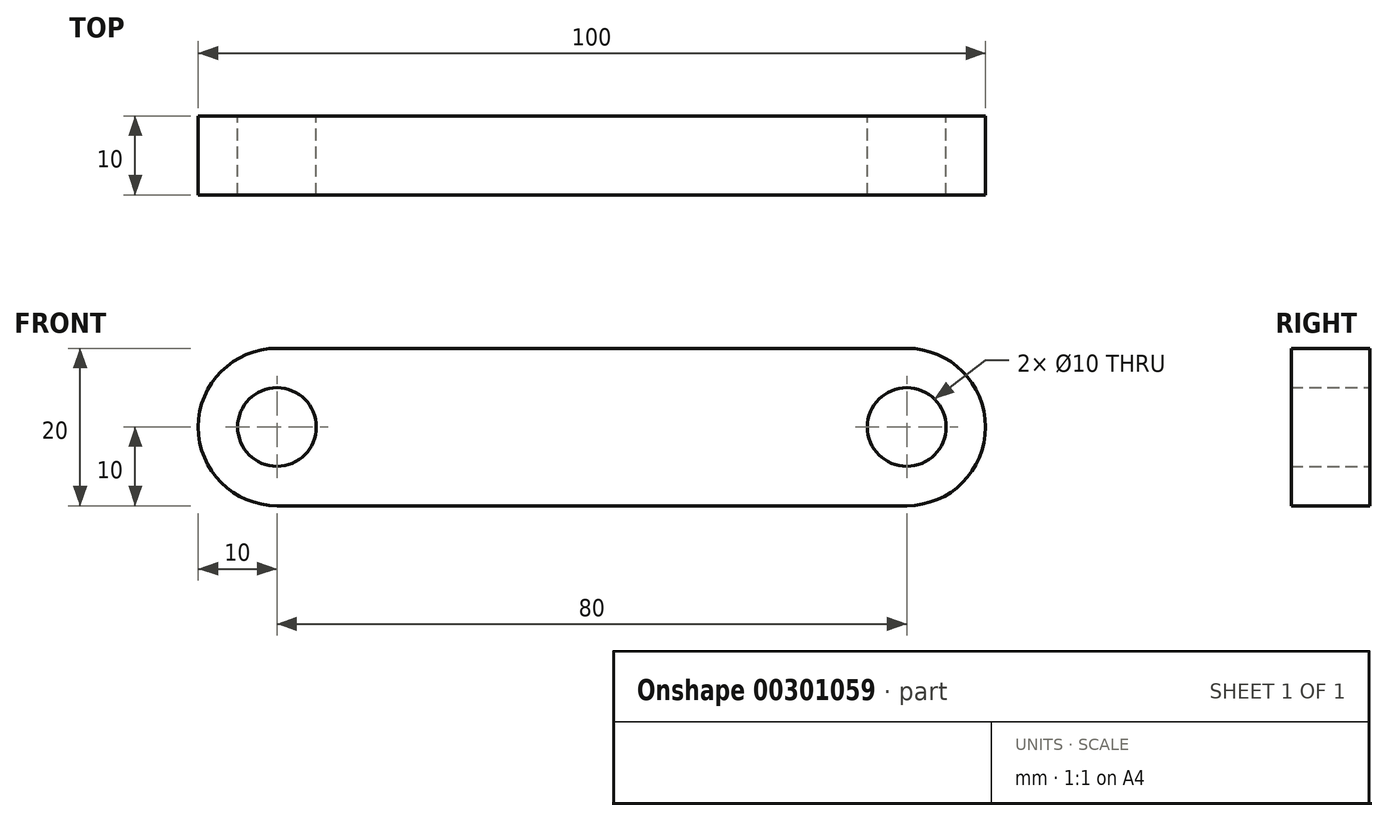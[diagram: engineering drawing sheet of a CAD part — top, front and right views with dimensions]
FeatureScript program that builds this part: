
annotation { "Feature Type Name" : "Feature", "Feature Type Description" : "" }
export const myFeature = defineFeature(function(context is Context, id is Id, definition is map)
    precondition{}
    {
        {
            var Q0;
            Q0=qCreatedBy(makeId("Front.planeOp"),FACE);
            var sketch = newSketch(context, id + "F0", { "sketchPlane" : qUnion([Q0])});
            skLineSegment(sketch, "E0", {"start": v(0, 10) * mm, "end": v(80, 10) * mm});
            skLineSegment(sketch, "E1", {"start": v(0, -10) * mm, "end": v(80, -10) * mm});
            skArc(sketch, "E2", {"start": v(0, 10) * mm, "mid": v(-10, 0) * mm, "end": v(0, -10) * mm});
            skArc(sketch, "E3", {"start": v(80, 10) * mm, "mid": v(90, 0) * mm, "end": v(80, -10) * mm});
            skCircle(sketch, "E4", {"center": v(0, 0) * mm, "radius": 5 * mm});
            skCircle(sketch, "E5", {"center": v(80, 0) * mm, "radius": 5 * mm});
            skSolve(sketch);
        }
        {
            var Q0;
            Q0 = qSketchRegion(id + "F0", true);
            extrude(context, id + "F1", {"entities" : qUnion([Q0]), "depth" : 10 * mm});
        }
    });
